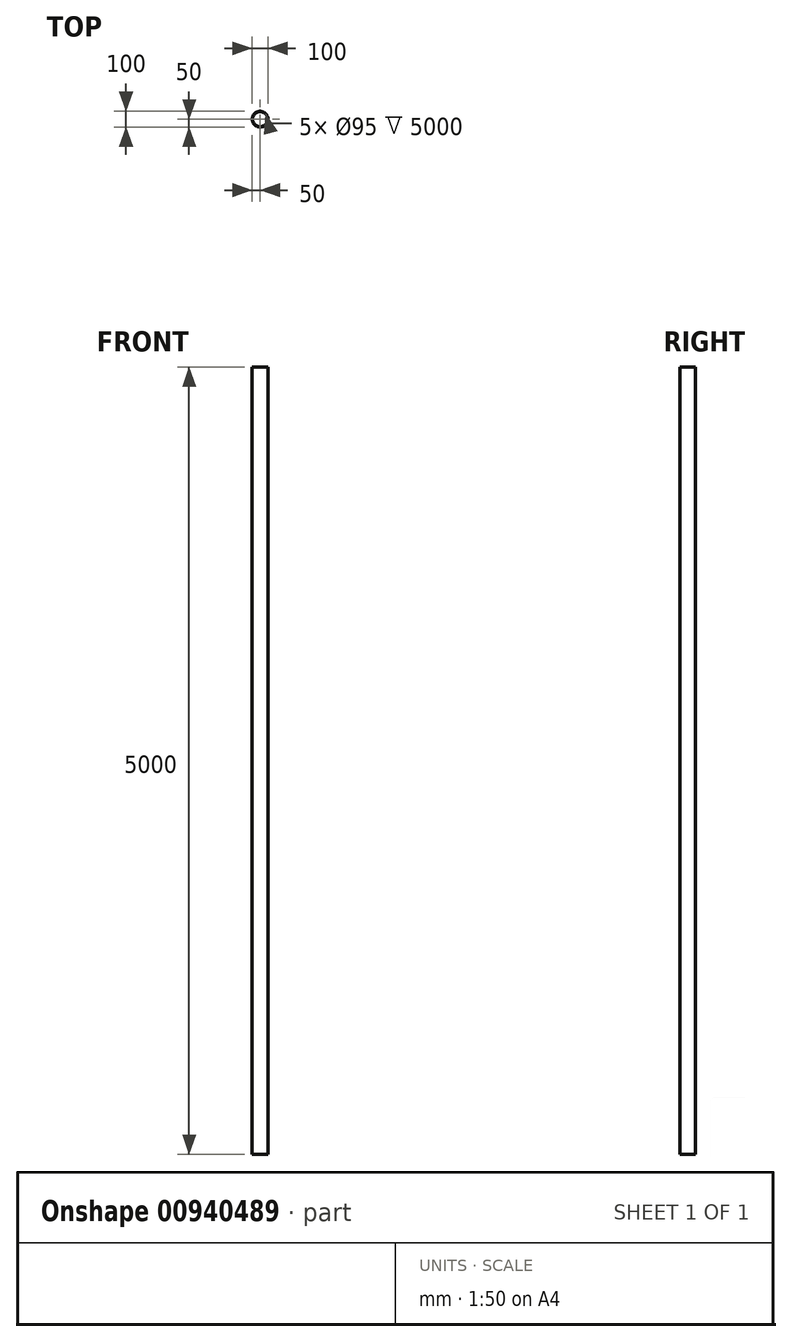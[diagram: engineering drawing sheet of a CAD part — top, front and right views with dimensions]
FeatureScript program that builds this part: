
annotation { "Feature Type Name" : "Feature", "Feature Type Description" : "" }
export const myFeature = defineFeature(function(context is Context, id is Id, definition is map)
    precondition{}
    {
        {
            var Q0;
            Q0=qCreatedBy(makeId("Top.planeOp"),FACE);
            var sketch = newSketch(context, id + "F0", { "sketchPlane" : qUnion([Q0])});
            skCircle(sketch, "E0", {"center": v(0, 0) * mm, "radius": 50 * mm});
            skSolve(sketch);
        }
        {
            var Q0;
            Q0=qSketchRegion(id+"F0",true);
            extrude(context, id + "F1", {"entities" : qUnion([Q0]), "depth" : 5000 * mm, "offsetDistance" : 25 * mm});
        }
        {
            var Q0;
            Q0=makeQuery(id+"F1.opExtrude","CAP_FACE",FACE,{"disambiguationData":[OSD([sQuery(id+"F0.wireOp",EDGE,"E0")])],"isStart":false});
            var Q1;
            Q1=makeQuery(id+"F1.opExtrude","CAP_FACE",FACE,{"disambiguationData":[OSD([sQuery(id+"F0.wireOp",EDGE,"E0")])],"isStart":true});
            var Q2;
            Q2=makeQuery(id+"F1.opExtrude","SWEPT_BODY",BODY,{"disambiguationData":[OSD([sQuery(id+"F0.wireOp",EDGE,"E0")])]});
            shell(context, id + "F2", {"entities" : qUnion([Q0, Q1]), "parts" : qUnion([Q2]), "thickness" : 2.5 * mm});
        }
    });
